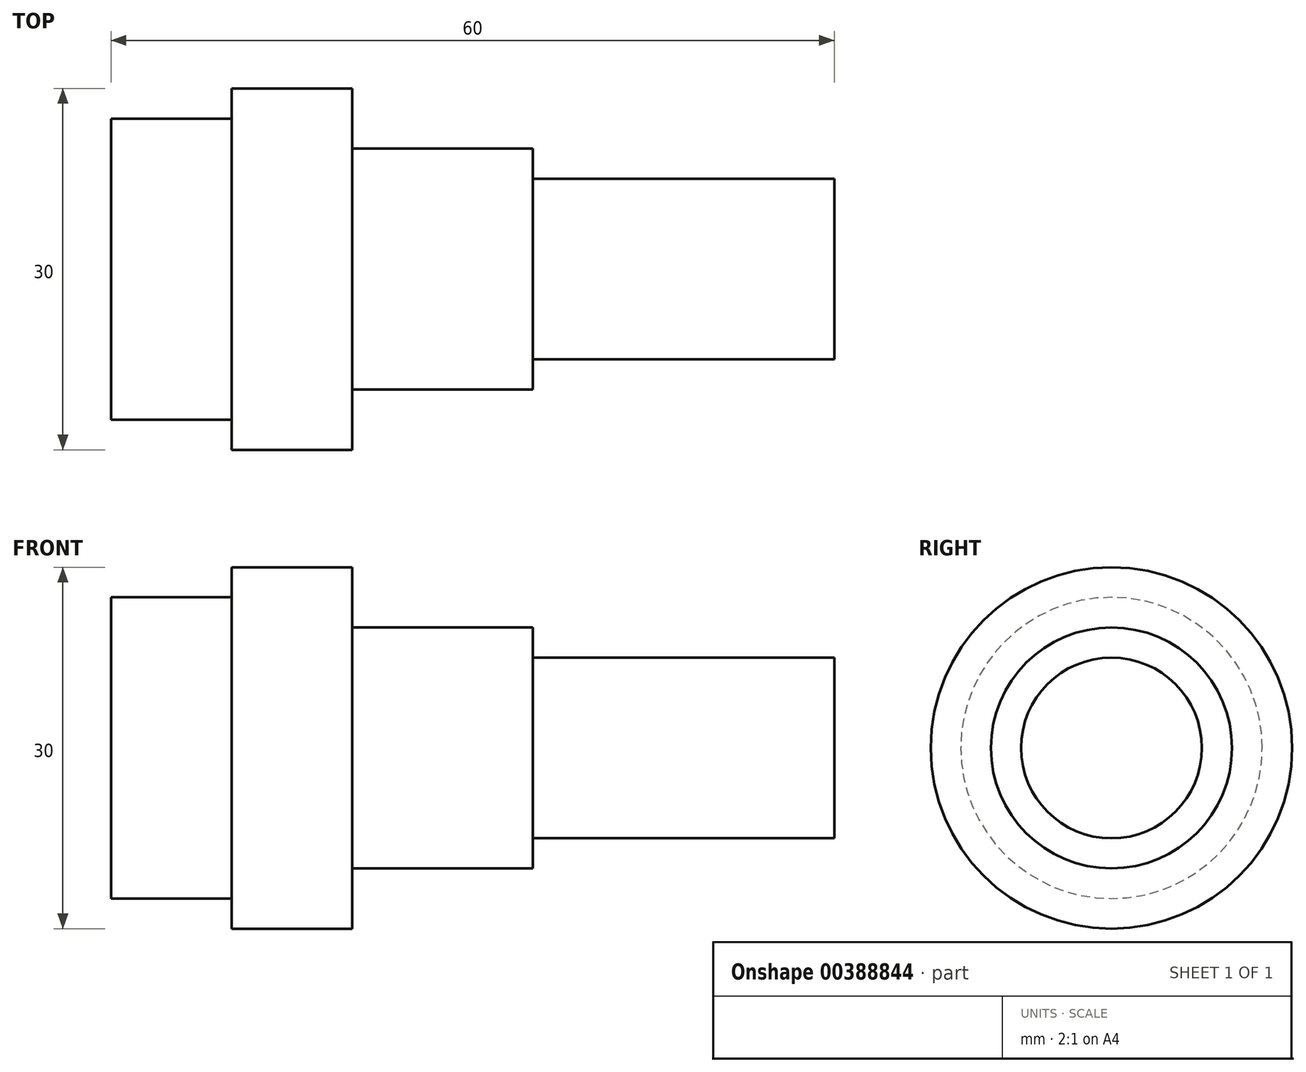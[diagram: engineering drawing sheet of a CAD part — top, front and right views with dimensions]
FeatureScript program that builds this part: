
annotation { "Feature Type Name" : "Feature", "Feature Type Description" : "" }
export const myFeature = defineFeature(function(context is Context, id is Id, definition is map)
    precondition{}
    {
        {
            var Q0;
            Q0=qCreatedBy(makeId("Front.planeOp"),FACE);
            var sketch = newSketch(context, id + "F0", { "sketchPlane" : qUnion([Q0])});
            skLineSegment(sketch, "E0", {"start": v(0, 0) * mm, "end": v(0, 7.5) * mm});
            skLineSegment(sketch, "E1", {"start": v(0, 7.5) * mm, "end": v(-25, 7.5) * mm});
            skLineSegment(sketch, "E2", {"start": v(-25, 7.5) * mm, "end": v(-25, 10) * mm});
            skLineSegment(sketch, "E3", {"start": v(-25, 10) * mm, "end": v(-40, 10) * mm});
            skLineSegment(sketch, "E4", {"start": v(-40, 10) * mm, "end": v(-40, 15) * mm});
            skLineSegment(sketch, "E5", {"start": v(-40, 15) * mm, "end": v(-50, 15) * mm});
            skLineSegment(sketch, "E6", {"start": v(-50, 15) * mm, "end": v(-50, 12.5) * mm});
            skLineSegment(sketch, "E7", {"start": v(-50, 12.5) * mm, "end": v(-60, 12.5) * mm});
            skLineSegment(sketch, "E8", {"start": v(-60, 12.5) * mm, "end": v(-60, 0) * mm});
            skLineSegment(sketch, "E9", {"start": v(-36.7, 0) * mm, "end": v(5.9, 0) * mm, "construction": true});
            skLineSegment(sketch, "E10", {"start": v(-60, 0) * mm, "end": v(0, 0) * mm});
            skSolve(sketch);
        }
        {
            var Q0;
            Q0=makeQuery(id+"F0.imprint","IMPRINT",FACE,{"disambiguationData":[TD([[makeQuery(id+"F0.imprint","IMPRINT",EDGE,{"derivedFrom":sQuery(id+"F0.wireOp",EDGE,"E0")}),1.0]])]});
            var Q1;
            Q1=sQuery(id+"F0.wireOp",EDGE,"E10");
            revolve(context, id + "F1", {"entities" : qUnion([Q0]), "axis" : qUnion([Q1]), "revolveType" : RevolveType.FULL});
        }
    });
